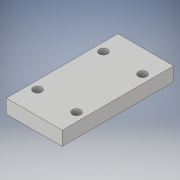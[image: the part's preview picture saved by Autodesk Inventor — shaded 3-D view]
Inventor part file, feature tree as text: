
AUTODESK INVENTOR PART (.ipt)
format: ipt  version: 2019 (Build 230136000, 136)  size: 112,128 bytes
history: native  units: in
note: dims shown in document units (in); Inventor stores cm internally (conversion verified against a paired STEP export)
features: sketch x2, extrude x1, hole x1, projected_geometry x1
ambient origin geometry x8: Origin, YZ Plane, XZ Plane, XY Plane, X Axis, Y Axis, Z Axis, Center Point
bodies: Solid1 (feature_tree)
feature tree (5):
  extrude  "Extrusion1"  Depth=1.0in
  hole  "Hole1"  [1 undecoded]
  sketch  "Sketch1"  dims[d0=2.0in d1=1.0in]
  sketch  "Sketch2"  dims[d2=0.25in d3=0.0in d4=1.181in d5=2.0in d6=0.4095in d9=1.181in d10=0.15in d11=0.15in d12=0.15in d13=0.15in d14=0.4095in d15=0.15in d16=0.75in d17=0.375in d18=0.25in d19=0.5635in d20=1.0in d21=0.8108in]
  projected_geometry  "Projected Loop1"
note: 1 required parameter value undecoded (feature->parameter linkage not recoverable at this tier; creation-order binding heuristic only, values carry confidence <= 0.55)
